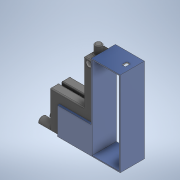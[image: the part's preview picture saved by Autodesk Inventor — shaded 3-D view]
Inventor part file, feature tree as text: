
AUTODESK INVENTOR PART (.ipt)
format: ipt  version: 2021 (Build 250183000, 183)  size: 314,368 bytes
history: native  units: mm
features: extrude x9, sketch x9, fillet x2
ambient origin geometry x8: Origin, YZ Plane, XZ Plane, XY Plane, X Axis, Y Axis, Z Axis, Center Point
bodies: Solid1 (feature_tree)
feature tree (20):
  extrude  "Extrusion1"  Depth=175.0mm
  extrude  "Extrusion2"  Depth=50.0mm TaperAngle=0.0deg
  extrude  "Extrusion3"  Depth=70.0mm TaperAngle=0.0deg
  extrude  "Extrusion4"  Depth=18.0mm
  extrude  "Extrusion5"  Depth=56.274mm TaperAngle=0.0deg
  extrude  "Extrusion6"  Depth=2.0mm TaperAngle=0.0deg
  fillet  "Fillet1"  Radius=2.0mm
  extrude  "Extrusion7"  Depth=20.704mm
  fillet  "Fillet2"  Radius=20.704155mm
  extrude  "Extrusion8"  Depth=10.0mm TaperAngle=0.0deg
  extrude  "Extrusion9"  Depth=9.53mm
  sketch  "Sketch1"  dims[d0=60.0mm d1=175.0mm]
  sketch  "Sketch2"  dims[d2=2.0mm d3=50.0mm d4=0.0mm]
  sketch  "Sketch3"  dims[d5=20.0mm d6=0.0mm d7=70.0mm d8=0.0mm]
  sketch  "Sketch4"  dims[d9=18.0mm d10=18.0mm]
  sketch  "Sketch5"  dims[d11=90.0mm d12=0.0mm d13=56.274mm d14=0.0mm]
  sketch  "Sketch6"  dims[d15=9.0mm d16=25.0mm d17=0.0mm d18=2.0mm]
  sketch  "Sketch7"  dims[d19=14.0mm d20=20.704mm d21=20.704155mm]
  sketch  "Sketch8"  dims[d22=10.0mm d23=18.0mm d24=0.0mm]
  sketch  "Sketch9"  dims[d25=2.0mm d26=11.56mm d27=8.0mm d28=9.0mm d29=0.0mm d30=0.0mm d31=7.0mm d32=10.0mm d33=20.3mm d34=9.53mm d35=0.0mm d36=0.0mm]
